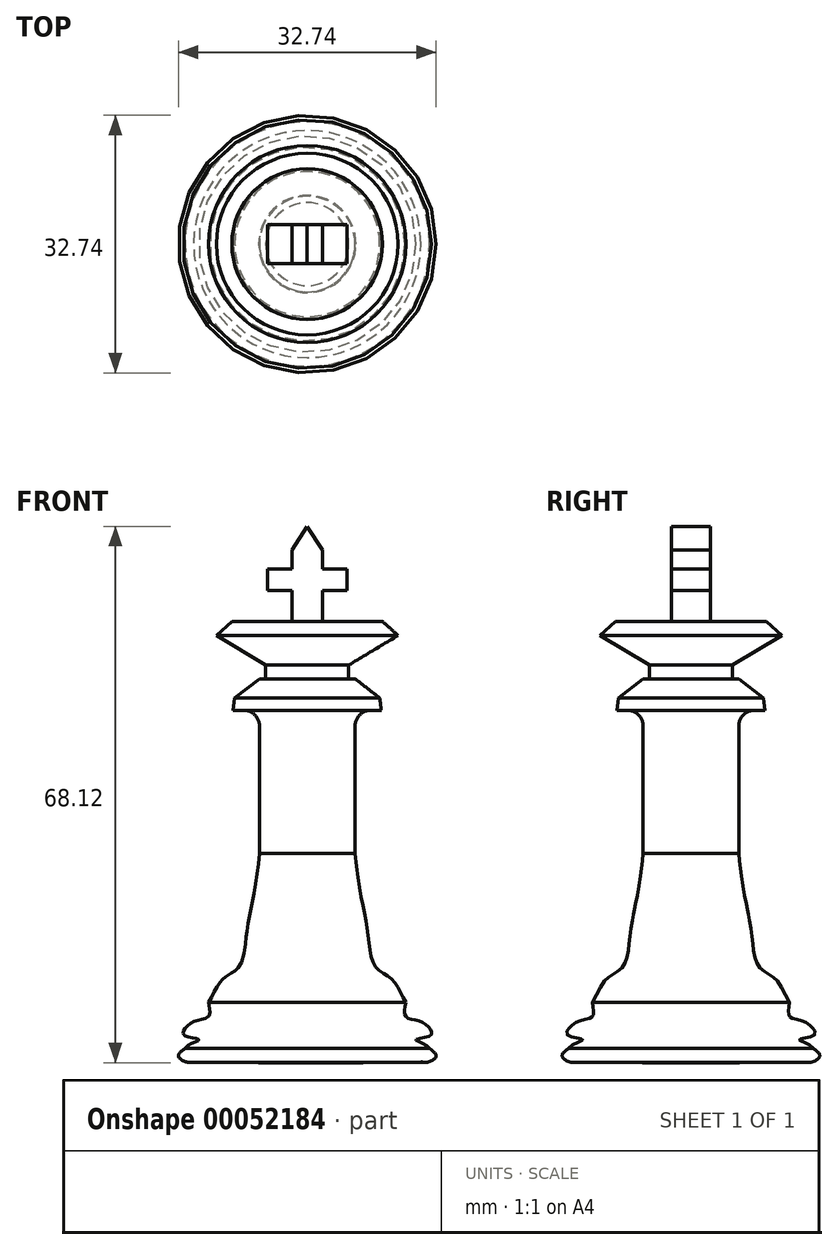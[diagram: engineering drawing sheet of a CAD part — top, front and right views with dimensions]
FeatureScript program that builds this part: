
annotation { "Feature Type Name" : "Feature", "Feature Type Description" : "" }
export const myFeature = defineFeature(function(context is Context, id is Id, definition is map)
    precondition{}
    {
        {
            var Q0;
            Q0=qCreatedBy(makeId("Front.planeOp"),FACE);
            var sketch = newSketch(context, id + "F0", { "sketchPlane" : qUnion([Q0])});
            skLineSegment(sketch, "E0.bottom", {"start": v(0, 26.82) * mm, "end": v(-6.07, 26.82) * mm});
            skLineSegment(sketch, "E0.top", {"start": v(0, -21.95) * mm, "end": v(-6.17, -21.95) * mm});
            skLineSegment(sketch, "E0.left", {"start": v(0, 26.82) * mm, "end": v(0, -21.95) * mm});
            skLineSegment(sketch, "E0.right", {"start": v(-6.07, 26.82) * mm, "end": v(-6.07, 4.6) * mm});
            skLineSegment(sketch, "E1", {"start": v(-6.07, 26.82) * mm, "end": v(-9.2, 24.38) * mm});
            skLineSegment(sketch, "E2", {"start": v(-9.2, 24.38) * mm, "end": v(-9.4, 22.82) * mm});
            skLineSegment(sketch, "E3", {"start": v(-9.4, 22.82) * mm, "end": v(-6.07, 22.82) * mm});
            skLineSegment(sketch, "E4", {"start": v(-6.07, 22.82) * mm, "end": v(-6.07, 26.82) * mm});
            skLineSegment(sketch, "E5", {"start": v(-6.07, -14.27) * mm, "end": v(-6.17, -21.95) * mm});
            skPoint(sketch, "E6.1.internal.snap0", {"position": v(-9.3, -14.27) * mm});
            skPoint(sketch, "E7.1.internal.snap0", {"position": v(-10.85, -21.06) * mm});
            skFitSpline(sketch, "E7", {"points": [v(-12.53, -14.27) * mm, v(-10.85, -11.46) * mm, v(-8.62, -9.7) * mm, v(-7.64, -5) * mm, v(-6.07, 4.6) * mm], "startDerivative": vector(8.85, 12.63) * mm, "endDerivative": vector(3.32, 39) * mm});
            skPoint(sketch, "E8.start.orphan", {"position": v(-15.63, -17.73) * mm});
            skPoint(sketch, "E9.start.orphan", {"position": v(-15.63, -18.5) * mm});
            skPoint(sketch, "E10.orphan", {"position": v(-15.54, -20.16) * mm});
            skFitSpline(sketch, "E11", {"points": [v(-12.53, -14.27) * mm, v(-12.53, -16.09) * mm, v(-14.15, -16.64) * mm, v(-15.63, -17.73) * mm, v(-15.63, -18.5) * mm, v(-13.78, -19.05) * mm, v(-15.54, -20.16) * mm, v(-14.43, -21.36) * mm, v(-12.53, -20.16) * mm, v(-6.17, -21.95) * mm], "startDerivative": vector(4.35, -21.12) * mm, "endDerivative": vector(37.5, -4.8) * mm});
            skLineSegment(sketch, "E12", {"start": v(-6.17, -21.95) * mm, "end": v(-14.43, -21.85) * mm});
            skFitSpline(sketch, "E13", {"points": [v(-14.43, -21.85) * mm, v(-15.44, -21.85) * mm, v(-16.37, -21.08) * mm, v(-15.54, -20.16) * mm], "startDerivative": vector(-3.06, -0.55) * mm, "endDerivative": vector(3.74, 2.62) * mm});
            skSolve(sketch);
        }
        {
            var Q0;
            Q0 = qSketchRegion(id + "F0", true);
            var Q1;
            Q1=sQuery(id+"F0.wireOp",EDGE,"E0.left");
            revolve(context, id + "F1", {"entities" : qUnion([Q0]), "axis" : qUnion([Q1]), "revolveType" : RevolveType.FULL});
        }
        {
            var Q0;
            Q0=qCreatedBy(makeId("Front.planeOp"),FACE);
            var sketch = newSketch(context, id + "F2", { "sketchPlane" : qUnion([Q0])});
            skLineSegment(sketch, "E14", {"start": v(0, 26.65) * mm, "end": v(-5.27, 26.65) * mm});
            skLineSegment(sketch, "E15", {"start": v(-5.27, 26.65) * mm, "end": v(-5.27, 28.56) * mm});
            skLineSegment(sketch, "E16", {"start": v(-9.58, 34.1) * mm, "end": v(0, 34.1) * mm});
            skLineSegment(sketch, "E17", {"start": v(0, 34.1) * mm, "end": v(0, 26.65) * mm});
            skLineSegment(sketch, "E18", {"start": v(-9.58, 34.1) * mm, "end": v(-11.54, 32.33) * mm});
            skLineSegment(sketch, "E19", {"start": v(-11.54, 32.33) * mm, "end": v(-5.27, 28.56) * mm});
            skSolve(sketch);
        }
        {
            var Q0;
            Q0 = qSketchRegion(id + "F2", true);
            var Q1;
            Q1=sQuery(id+"F2.wireOp",EDGE,"E17");
            revolve(context, id + "F3", {"operationType" : NewBodyOperationType.ADD, "entities" : qUnion([Q0]), "axis" : qUnion([Q1]), "revolveType" : RevolveType.FULL});
        }
        {
            var Q0;
            Q0=qCreatedBy(makeId("Front.planeOp"),FACE);
            var sketch = newSketch(context, id + "F4", { "sketchPlane" : qUnion([Q0])});
            skLineSegment(sketch, "E20", {"start": v(0, 33.49) * mm, "end": v(0, 40.75) * mm});
            skLineSegment(sketch, "E21", {"start": v(0, 40.75) * mm, "end": v(0, 46.17) * mm});
            skLineSegment(sketch, "E22", {"start": v(0, 46.17) * mm, "end": v(-1.93, 43.14) * mm});
            skLineSegment(sketch, "E23", {"start": v(-1.93, 43.14) * mm, "end": v(-1.93, 40.75) * mm});
            skLineSegment(sketch, "E24", {"start": v(-1.93, 40.75) * mm, "end": v(-5.07, 40.75) * mm});
            skLineSegment(sketch, "E25", {"start": v(-5.07, 40.75) * mm, "end": v(-5.07, 38) * mm});
            skLineSegment(sketch, "E26", {"start": v(-5.07, 38) * mm, "end": v(-1.95, 38) * mm});
            skLineSegment(sketch, "E27", {"start": v(-1.95, 38) * mm, "end": v(-1.95, 33.49) * mm});
            skLineSegment(sketch, "E28", {"start": v(-1.95, 33.49) * mm, "end": v(0, 33.49) * mm});
            skLineSegment(sketch, "E29.MirrorCS", {"start": v(5.07, 38) * mm, "end": v(1.95, 38) * mm});
            skLineSegment(sketch, "E30.MirrorCS", {"start": v(1.95, 38) * mm, "end": v(1.95, 33.49) * mm});
            skLineSegment(sketch, "E31.MirrorCS", {"start": v(1.95, 33.49) * mm, "end": v(0, 33.49) * mm});
            skLineSegment(sketch, "E32.MirrorCS", {"start": v(5.07, 40.75) * mm, "end": v(5.07, 38) * mm});
            skLineSegment(sketch, "E33.MirrorCS", {"start": v(1.93, 40.75) * mm, "end": v(5.07, 40.75) * mm});
            skLineSegment(sketch, "E34.MirrorCS", {"start": v(0, 46.17) * mm, "end": v(1.93, 43.14) * mm});
            skLineSegment(sketch, "E35.MirrorCS", {"start": v(1.93, 43.14) * mm, "end": v(1.93, 40.75) * mm});
            skSolve(sketch);
        }
        {
            var Q0;
            Q0 = qSketchRegion(id + "F4", true);
            extrude(context, id + "F5", {"entities" : qUnion([Q0]), "operationType" : NewBodyOperationType.ADD, "endBound" : BoundingType.SYMMETRIC, "depth" : 5 * mm});
        }
        {
            var Q0;
            Q0 = qSketchRegion(id + "F4", true);
            extrude(context, id + "F6", {"entities" : qUnion([Q0]), "operationType" : NewBodyOperationType.ADD, "endBound" : BoundingType.SYMMETRIC, "oppositeDirection" : true, "depth" : 5 * mm});
        }
        {
            var Q0;
            Q0=makeQuery(id+"F1.opRevolve","SWEPT_EDGE",EDGE,{"disambiguationData":[OSD([sQuery(id+"F0.wireOp",EDGE,"E0.right"),sQuery(id+"F0.wireOp",EDGE,"E3"),sQuery(id+"F0.wireOp",EDGE,"E4")])]});
            fillet(context, id + "F7", {"entities" : qUnion([Q0]), "radius" : 2 * mm, "tangentPropagation" : true, "allowEdgeOverflow" : false});
        }
    });
